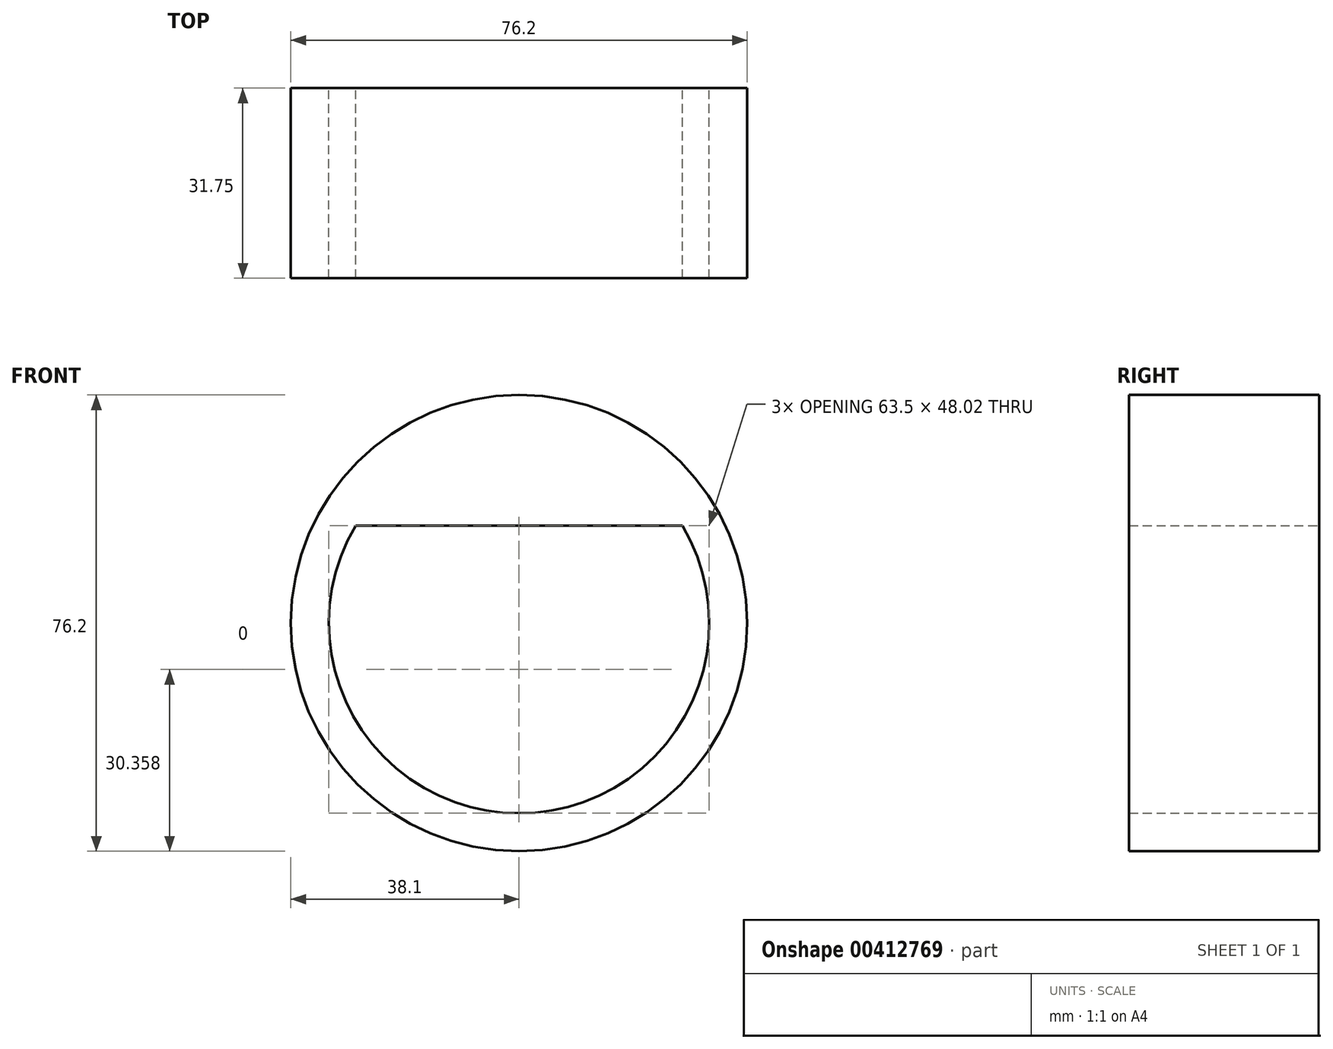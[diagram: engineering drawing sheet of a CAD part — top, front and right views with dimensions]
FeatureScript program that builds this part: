
annotation { "Feature Type Name" : "Feature", "Feature Type Description" : "" }
export const myFeature = defineFeature(function(context is Context, id is Id, definition is map)
    precondition{}
    {
        {
            var Q0;
            Q0=qCreatedBy(makeId("Front.planeOp"),FACE);
            var sketch = newSketch(context, id + "F0", { "sketchPlane" : qUnion([Q0])});
            skCircle(sketch, "E0", {"center": v(0, 0) * mm, "radius": 38.1 * mm});
            skArc(sketch, "E1", {"start": v(-27.27, 16.27) * mm, "mid": v(0, -31.75) * mm, "end": v(27.27, 16.27) * mm});
            skLineSegment(sketch, "E2", {"start": v(-27.27, 16.27) * mm, "end": v(27.27, 16.27) * mm});
            skSolve(sketch);
        }
        {
            var Q0;
            Q0 = qSketchRegion(id + "F0", true);
            extrude(context, id + "F1", {"entities" : qUnion([Q0]), "depth" : 31.75 * mm, "offsetDistance" : 25.4 * mm});
        }
    });
